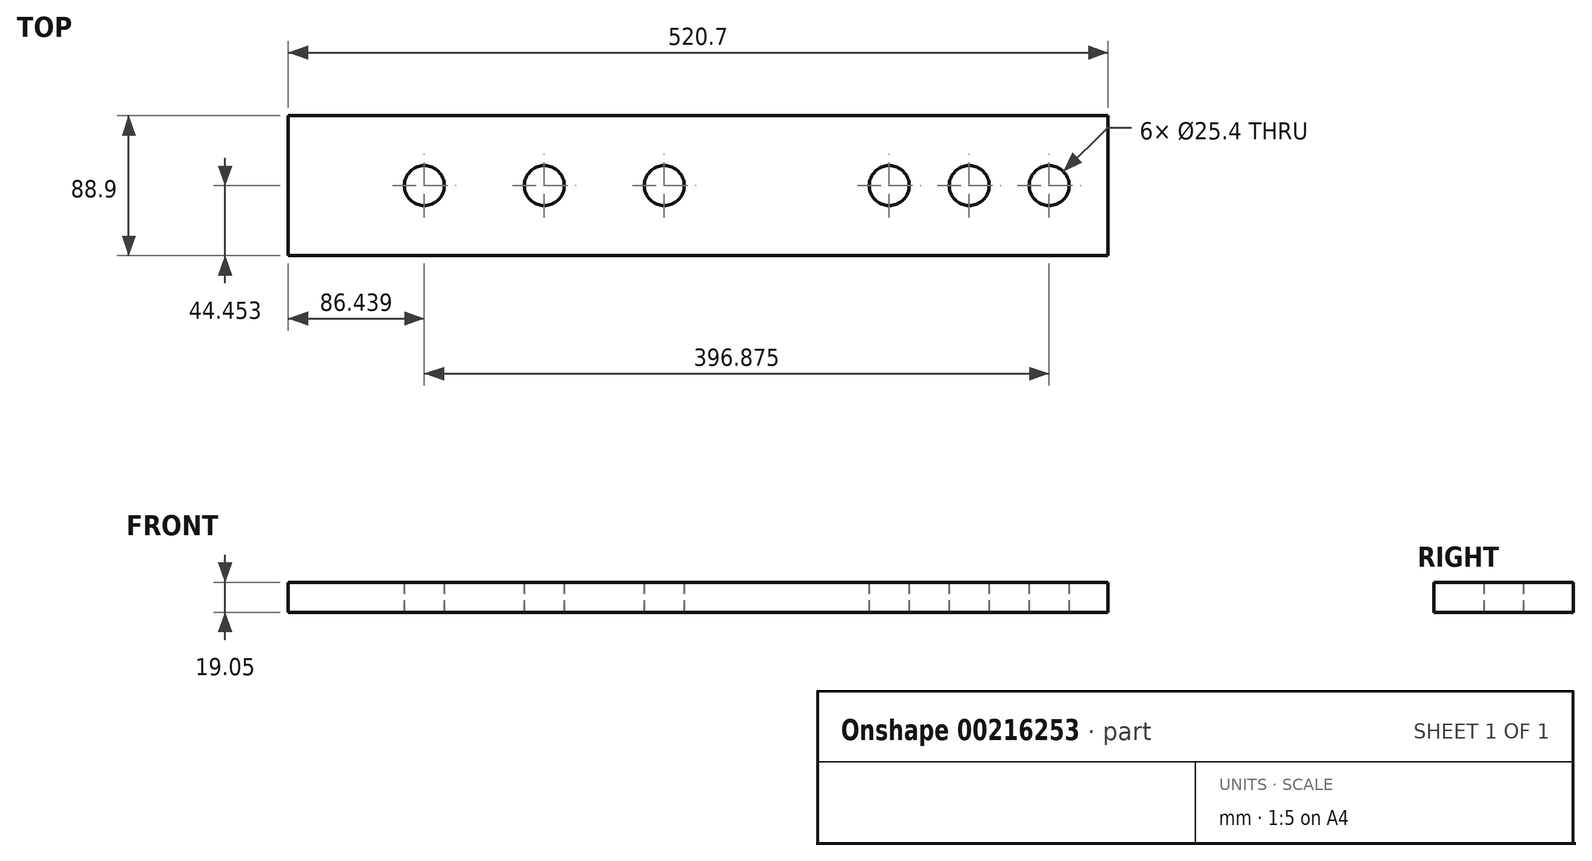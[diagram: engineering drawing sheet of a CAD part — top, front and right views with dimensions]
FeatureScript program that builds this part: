
annotation { "Feature Type Name" : "Feature", "Feature Type Description" : "" }
export const myFeature = defineFeature(function(context is Context, id is Id, definition is map)
    precondition{}
    {
        {
            var Q0;
            Q0=qCreatedBy(makeId("Top.planeOp"),FACE);
            var sketch = newSketch(context, id + "F0", { "sketchPlane" : qUnion([Q0])});
            skLineSegment(sketch, "E0", {"start": v(-3261.76, -2625.4) * mm, "end": v(-2741.06, -2625.4) * mm});
            skLineSegment(sketch, "E1", {"start": v(-2741.06, -2625.4) * mm, "end": v(-2741.06, -2536.5) * mm});
            skLineSegment(sketch, "E2", {"start": v(-2741.06, -2536.5) * mm, "end": v(-3261.76, -2536.5) * mm});
            skLineSegment(sketch, "E3", {"start": v(-3261.76, -2536.5) * mm, "end": v(-3261.76, -2625.4) * mm});
            skCircle(sketch, "E4", {"center": v(-3099.12, -2580.96) * mm, "radius": 12.7 * mm});
            skCircle(sketch, "E5", {"center": v(-3022.92, -2580.96) * mm, "radius": 12.7 * mm});
            skCircle(sketch, "E6", {"center": v(-3175.32, -2580.96) * mm, "radius": 12.7 * mm});
            skCircle(sketch, "E7", {"center": v(-2829.25, -2580.96) * mm, "radius": 12.7 * mm});
            skCircle(sketch, "E8", {"center": v(-2880.05, -2580.96) * mm, "radius": 12.7 * mm});
            skCircle(sketch, "E9", {"center": v(-2778.45, -2580.96) * mm, "radius": 12.7 * mm});
            skSolve(sketch);
        }
        {
            var Q0;
            Q0=makeQuery(id+"F0.imprint","IMPRINT",FACE,{"disambiguationData":[TD([[makeQuery(id+"F0.imprint","IMPRINT",EDGE,{"derivedFrom":sQuery(id+"F0.wireOp",EDGE,"E0")}),1.0]])]});
            extrude(context, id + "F1", {"entities" : qUnion([Q0]), "depth" : 19.05 * mm});
        }
    });
